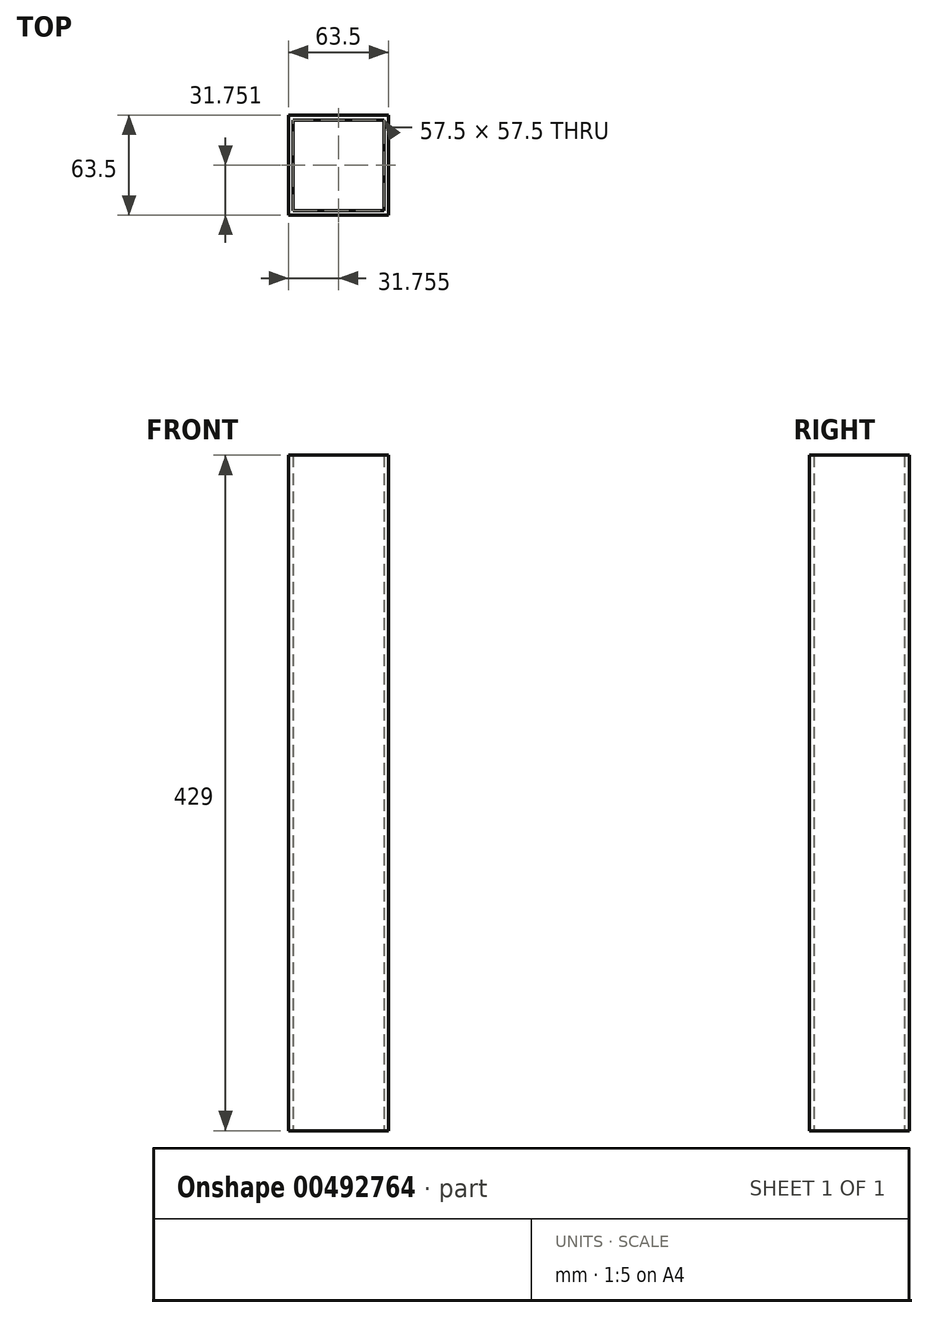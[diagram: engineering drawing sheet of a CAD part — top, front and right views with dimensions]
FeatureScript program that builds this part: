
annotation { "Feature Type Name" : "Feature", "Feature Type Description" : "" }
export const myFeature = defineFeature(function(context is Context, id is Id, definition is map)
    precondition{}
    {
        {
            var Q0;
            Q0=qCreatedBy(makeId("Top.planeOp"),FACE);
            var sketch = newSketch(context, id + "F0", { "sketchPlane" : qUnion([Q0])});
            skLineSegment(sketch, "E0.bottom", {"start": v(-25.8, 25.98) * mm, "end": v(31.7, 25.98) * mm});
            skLineSegment(sketch, "E0.top", {"start": v(-25.8, -31.52) * mm, "end": v(31.7, -31.52) * mm});
            skLineSegment(sketch, "E0.left", {"start": v(-25.8, 25.98) * mm, "end": v(-25.8, -31.52) * mm});
            skLineSegment(sketch, "E0.right", {"start": v(31.7, 25.98) * mm, "end": v(31.7, -31.52) * mm});
            skLineSegment(sketch, "E1.bottom", {"start": v(-28.8, 28.98) * mm, "end": v(34.7, 28.98) * mm});
            skLineSegment(sketch, "E1.top", {"start": v(-28.8, -34.52) * mm, "end": v(34.7, -34.52) * mm});
            skLineSegment(sketch, "E1.left", {"start": v(-28.8, 28.98) * mm, "end": v(-28.8, -34.52) * mm});
            skLineSegment(sketch, "E1.right", {"start": v(34.7, 28.98) * mm, "end": v(34.7, -34.52) * mm});
            skSolve(sketch);
        }
        {
            var Q0;
            Q0=qSketchRegion(id+"F0",true);
            extrude(context, id + "F1", {"entities" : qUnion([Q0]), "depth" : 429 * mm});
        }
    });
